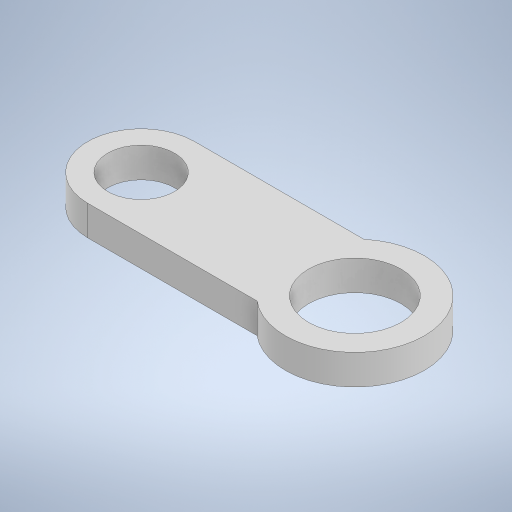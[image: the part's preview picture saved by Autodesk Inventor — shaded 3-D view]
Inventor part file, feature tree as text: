
AUTODESK INVENTOR PART (.ipt)
format: ipt  version: 2023 (Build 270158000, 158)  size: 240,128 bytes
history: native  units: in
note: dims shown in document units (in); Inventor stores cm internally (conversion verified against a paired STEP export)
features: extrude x1, sketch x1
ambient origin geometry x8: Origin, YZ Plane, XZ Plane, XY Plane, X Axis, Y Axis, Z Axis, Center Point
bodies: Solid1 (feature_tree)
feature tree (2):
  extrude  "Extrusion1"  Depth=0.281in TaperAngle=0.0deg
  sketch  "Sketch1"  dims[d4=0.625in d5=0.281in d6=0.0in d3=0.5in]
